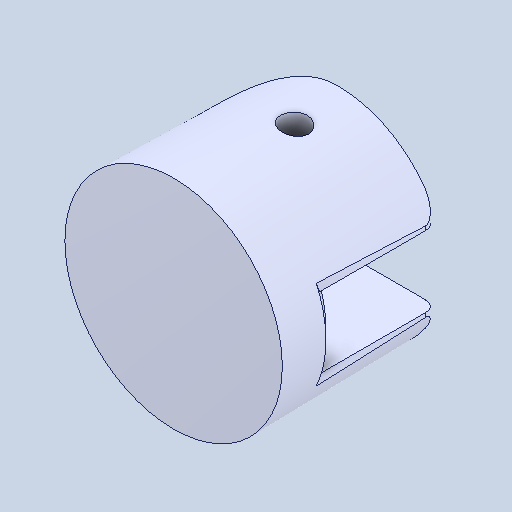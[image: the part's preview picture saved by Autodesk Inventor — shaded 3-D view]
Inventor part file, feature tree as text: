
AUTODESK INVENTOR PART (.ipt)
format: ipt  version: 2022 (Build 260153000, 153)  size: 141,824 bytes
history: mixed  units: mm
features: other x1, chamfer x1, imported_body x1
ambient origin geometry x8: Origin, YZ Plane, XZ Plane, XY Plane, X Axis, Y Axis, Z Axis, Center Point
bodies: Body1 (imported_parasolid)
feature tree (3):
  other  "Sólido1"
  chamfer  "Chamfer1"  [1 undecoded]
  imported_body  NMx_Import_Brep_tag  [imported B-rep: ~5 faces, bbox_mm=None]
note: 1 required parameter value undecoded (feature->parameter linkage not recoverable at this tier; creation-order binding heuristic only, values carry confidence <= 0.55)
